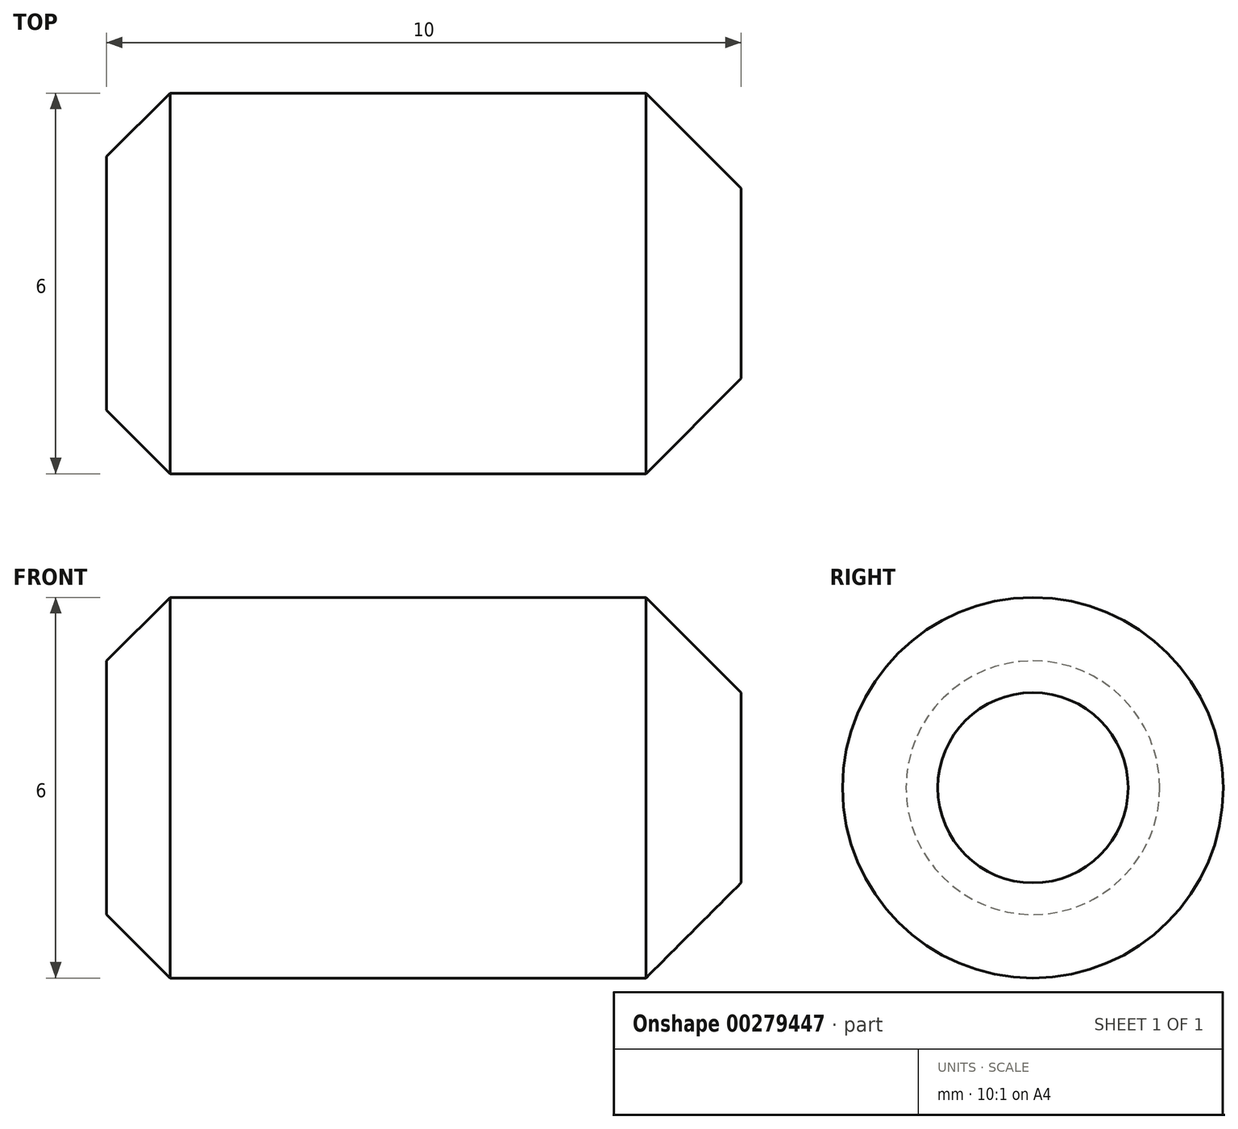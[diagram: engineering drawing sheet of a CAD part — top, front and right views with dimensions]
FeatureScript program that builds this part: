
annotation { "Feature Type Name" : "Feature", "Feature Type Description" : "" }
export const myFeature = defineFeature(function(context is Context, id is Id, definition is map)
    precondition{}
    {
        {
            var Q0;
            Q0=qCreatedBy(makeId("Right.planeOp"),FACE);
            var sketch = newSketch(context, id + "F0", { "sketchPlane" : qUnion([Q0])});
            skLineSegment(sketch, "E0", {"start": v(0, 0) * mm, "end": v(0, 3) * mm, "construction": true});
            skCircle(sketch, "E1", {"center": v(0, 3) * mm, "radius": 3 * mm});
            skSolve(sketch);
        }
        {
            var Q0;
            Q0=makeQuery(id+"F0.imprint","IMPRINT",FACE,{"disambiguationData":[TD([[makeQuery(id+"F0.imprint","IMPRINT",EDGE,{"derivedFrom":sQuery(id+"F0.wireOp",EDGE,"E1")}),1.0]])]});
            extrude(context, id + "F1", {"entities" : qUnion([Q0]), "depth" : 10 * mm});
        }
        {
            var Q0;
            Q0=makeQuery(id+"F1.opExtrude","CAP_EDGE",EDGE,{"disambiguationData":[OSD([sQuery(id+"F0.wireOp",EDGE,"E1")])],"isStart":false});
            chamfer(context, id + "F2", {"entities" : qUnion([Q0]), "width" : 1.5 * mm, "tangentPropagation" : true});
        }
        {
            var Q0;
            Q0=makeQuery(id+"F1.opExtrude","CAP_EDGE",EDGE,{"disambiguationData":[OSD([sQuery(id+"F0.wireOp",EDGE,"E1")])],"isStart":true});
            chamfer(context, id + "F3", {"entities" : qUnion([Q0]), "width" : 1 * mm, "tangentPropagation" : true});
        }
    });
